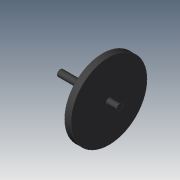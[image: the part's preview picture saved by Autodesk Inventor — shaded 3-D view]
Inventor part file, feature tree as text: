
AUTODESK INVENTOR PART (.ipt)
format: ipt  version: 2020 (Build 240168000, 168)  size: 91,648 bytes
history: native  units: mm
features: revolve x1, sketch x1
ambient origin geometry x8: Origin, YZ Plane, XZ Plane, XY Plane, X Axis, Y Axis, Z Axis, Center Point
bodies: Body1 (feature_tree)
feature tree (2):
  revolve  "Revolution1"  [1 undecoded]
  sketch  "Sketch2"  dims[d3=1.55mm d4=20.0mm d5=3.0mm d6=5.0mm d7=1.35mm d8=18.0mm d9=90.0deg]
note: 1 required parameter value undecoded (feature->parameter linkage not recoverable at this tier; creation-order binding heuristic only, values carry confidence <= 0.55)
